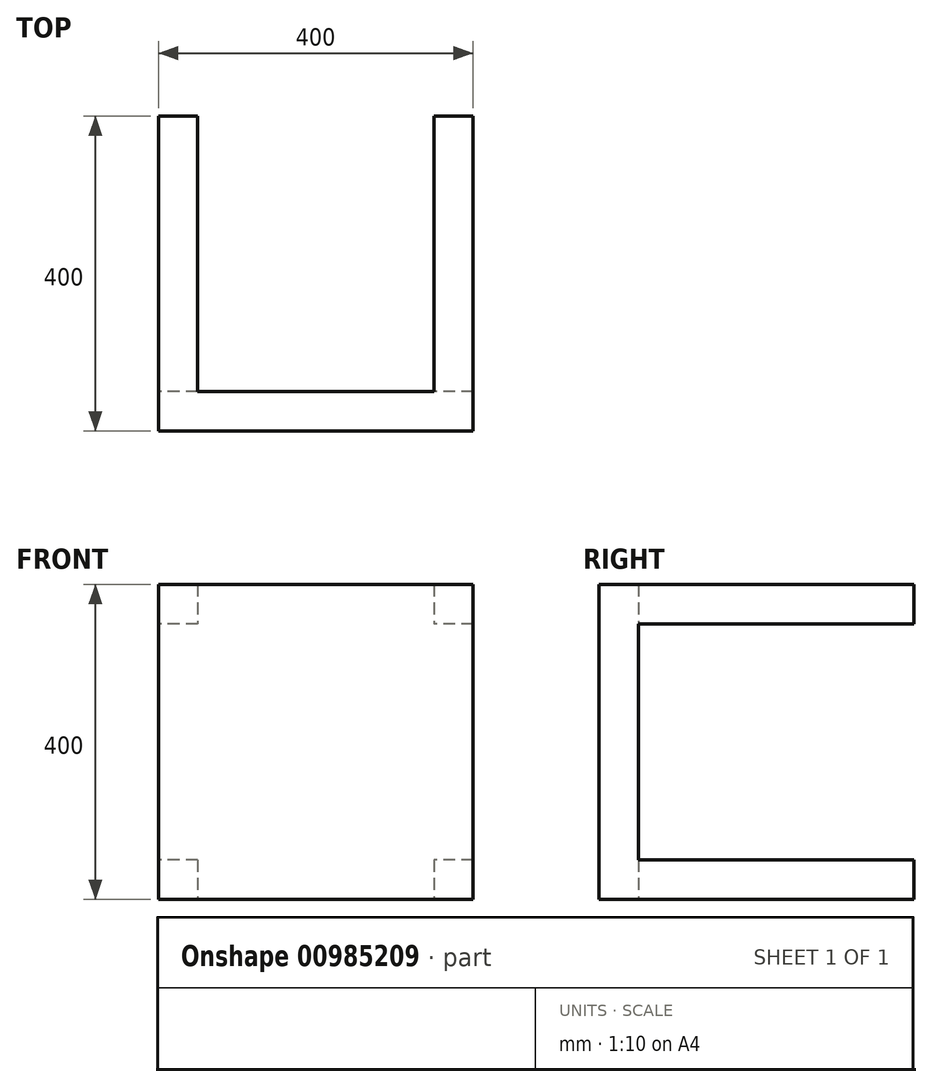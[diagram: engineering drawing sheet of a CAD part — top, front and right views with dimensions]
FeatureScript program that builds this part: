
annotation { "Feature Type Name" : "Feature", "Feature Type Description" : "" }
export const myFeature = defineFeature(function(context is Context, id is Id, definition is map)
    precondition{}
    {
        {
            var Q0;
            Q0=qCreatedBy(makeId("Top.planeOp"),FACE);
            var sketch = newSketch(context, id + "F0", { "sketchPlane" : qUnion([Q0])});
            skLineSegment(sketch, "E0.bottom", {"start": v(200, -200) * mm, "end": v(-200, -200) * mm});
            skLineSegment(sketch, "E0.top", {"start": v(200, 200) * mm, "end": v(-200, 200) * mm});
            skLineSegment(sketch, "E0.left", {"start": v(200, -200) * mm, "end": v(200, 200) * mm});
            skLineSegment(sketch, "E0.right", {"start": v(-200, -200) * mm, "end": v(-200, 200) * mm});
            skPoint(sketch, "E0.middle", {"position": v(0, 0) * mm});
            skLineSegment(sketch, "E1", {"start": v(-200, 200) * mm, "end": v(-150, 200) * mm});
            skLineSegment(sketch, "E2", {"start": v(-150, 200) * mm, "end": v(-150, -150) * mm});
            skLineSegment(sketch, "E3", {"start": v(-150, -150) * mm, "end": v(150, -150) * mm});
            skLineSegment(sketch, "E4", {"start": v(150, -150) * mm, "end": v(150, 200) * mm});
            skSolve(sketch);
        }
        {
            var Q0;
            Q0=makeQuery(id+"F0.imprint","IMPRINT",FACE,{"disambiguationData":[TD([[makeQuery(id+"F0.imprint","IMPRINT",EDGE,{"derivedFrom":sQuery(id+"F0.wireOp",EDGE,"E0.bottom")}),-1.0]])]});
            extrude(context, id + "F1", {"entities" : qUnion([Q0]), "depth" : 400 * mm, "offsetDistance" : 25 * mm});
        }
        {
            var Q0;
            Q0=makeQuery(id+"F1.opExtrude","SWEPT_FACE",FACE,{"disambiguationData":[OSD([sQuery(id+"F0.wireOp",EDGE,"E0.right")])]});
            var sketch = newSketch(context, id + "F2", { "sketchPlane" : qUnion([Q0])});
            skLineSegment(sketch, "E5", {"start": v(-200, 400) * mm, "end": v(-200, 350) * mm});
            skLineSegment(sketch, "E6", {"start": v(-200, 350) * mm, "end": v(150, 350) * mm});
            skLineSegment(sketch, "E7", {"start": v(150, 350) * mm, "end": v(150, 50) * mm});
            skLineSegment(sketch, "E8", {"start": v(150, 50) * mm, "end": v(-200, 50) * mm});
            skSolve(sketch);
        }
        {
            var Q0;
            {var subQ0=sQuery(id+"F2.wireOp",EDGE,"E6");Q0=makeQuery(id+"F2.imprint","IMPRINT",FACE,{"disambiguationData":[TD([[makeQuery(id+"F2.imprint","IMPRINT",EDGE,{"derivedFrom":subQ0}),-1.0]])]});}
            extrude(context, id + "F3", {"entities" : qUnion([Q0]), "operationType" : NewBodyOperationType.REMOVE, "endBound" : BoundingType.THROUGH_ALL, "oppositeDirection" : true, "depth" : 25 * mm, "offsetDistance" : 25 * mm});
        }
    });
